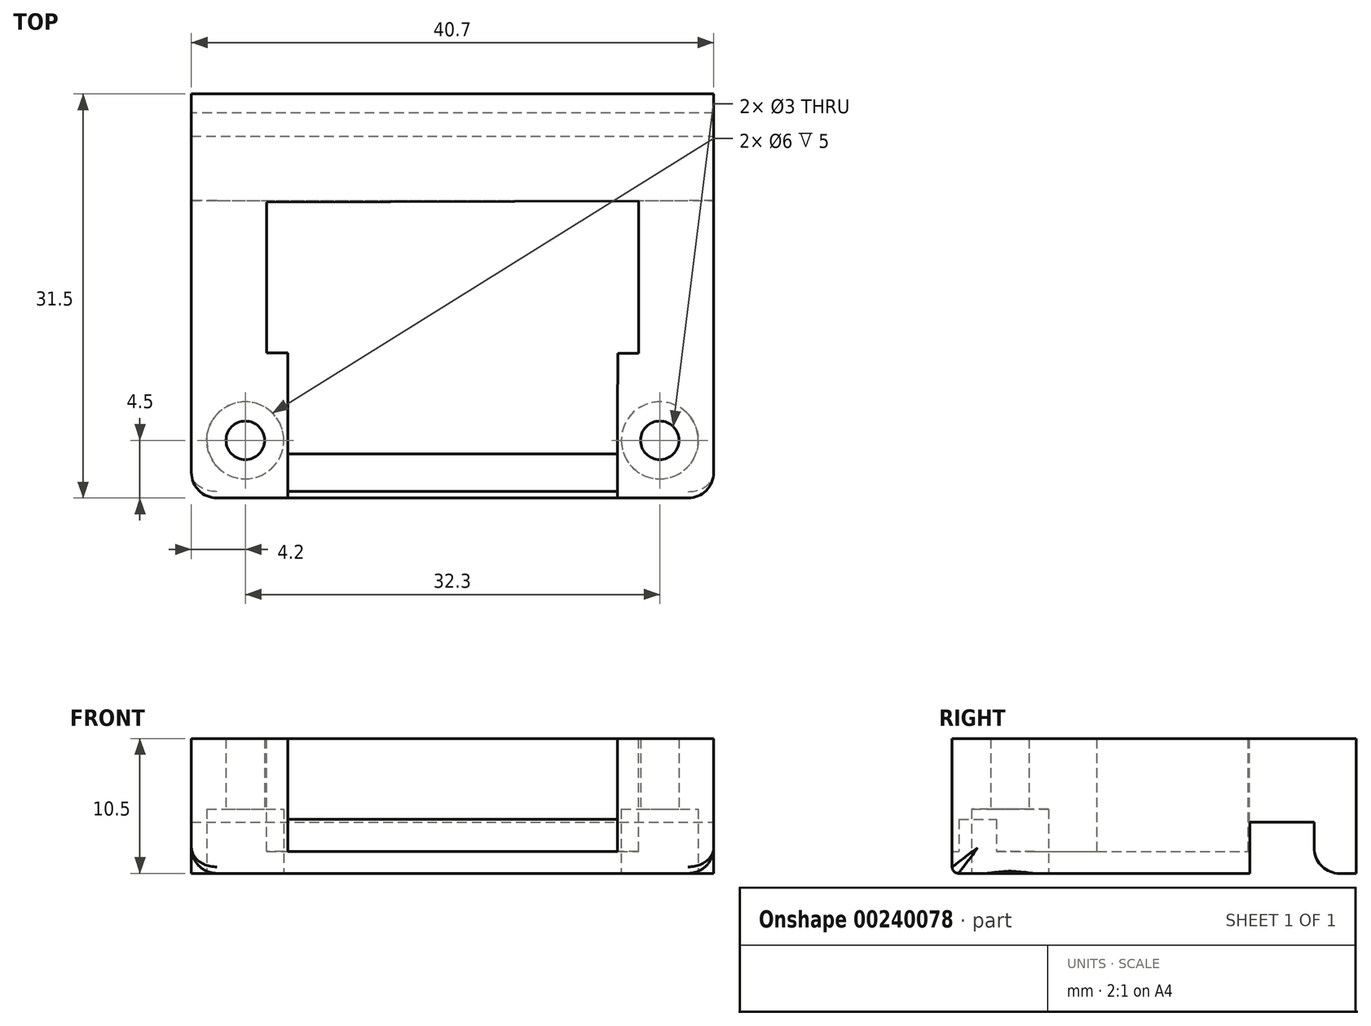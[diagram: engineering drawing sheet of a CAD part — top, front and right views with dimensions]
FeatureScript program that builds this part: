
annotation { "Feature Type Name" : "Feature", "Feature Type Description" : "" }
export const myFeature = defineFeature(function(context is Context, id is Id, definition is map)
    precondition{}
    {
        {
            var Q0;
            Q0=qCreatedBy(makeId("Top.planeOp"),FACE);
            var sketch = newSketch(context, id + "F0", { "sketchPlane" : qUnion([Q0])});
            skLineSegment(sketch, "E0.bottom", {"start": v(20.35, -15) * mm, "end": v(-20.35, -15) * mm});
            skLineSegment(sketch, "E0.top", {"start": v(20.35, 15) * mm, "end": v(-20.35, 15) * mm});
            skLineSegment(sketch, "E0.left", {"start": v(20.35, -15) * mm, "end": v(20.35, 15) * mm});
            skLineSegment(sketch, "E0.right", {"start": v(-20.35, -15) * mm, "end": v(-20.35, 15) * mm});
            skPoint(sketch, "E0.middle", {"position": v(0, 0) * mm});
            skPoint(sketch, "E1", {"position": v(16.15, -10.5) * mm});
            skPoint(sketch, "E2", {"position": v(-16.15, -10.5) * mm});
            skLineSegment(sketch, "E3", {"start": v(-20.35, 8.2) * mm, "end": v(20.35, 8.2) * mm});
            skLineSegment(sketch, "E4", {"start": v(-20.35, 13.2) * mm, "end": v(20.35, 13.2) * mm});
            skSolve(sketch);
        }
        {
            var Q0;
            Q0 = qSketchRegion(id + "F0", true);
            extrude(context, id + "F1", {"entities" : qUnion([Q0]), "depth" : 10.5 * mm});
        }
        {
            var Q0;
            Q0=sQuery(id+"F0.wireOp",VERTEX,"E2");
            var Q1;
            Q1=makeQuery(id+"F1.opExtrude","SWEPT_BODY",BODY,{"disambiguationData":[OSD([sQuery(id+"F0.wireOp",EDGE,"E0.bottom"),sQuery(id+"F0.wireOp",EDGE,"E0.top"),sQuery(id+"F0.wireOp",EDGE,"E0.left"),sQuery(id+"F0.wireOp",EDGE,"E0.right")])]});
            hole(context, id + "F2", {"style" : HoleStyle.C_BORE, "endStyle" : HoleEndStyle.THROUGH, "oppositeDirection" : true, "holeDiameter" : 3 * mm, "cBoreDiameter" : 6 * mm, "cBoreDepth" : 5 * mm, "locations" : qUnion([Q0]), "scope" : qUnion([Q1]), "isTappedThrough" : true});
        }
        {
            var Q0;
            Q0=sQuery(id+"F0.wireOp",VERTEX,"E1");
            var Q1;
            Q1=makeQuery(id+"F1.opExtrude","SWEPT_BODY",BODY,{"disambiguationData":[OSD([sQuery(id+"F0.wireOp",EDGE,"E0.bottom"),sQuery(id+"F0.wireOp",EDGE,"E0.top"),sQuery(id+"F0.wireOp",EDGE,"E0.left"),sQuery(id+"F0.wireOp",EDGE,"E0.right")])]});
            hole(context, id + "F3", {"style" : HoleStyle.C_BORE, "endStyle" : HoleEndStyle.THROUGH, "oppositeDirection" : true, "holeDiameter" : 3 * mm, "cBoreDiameter" : 6 * mm, "cBoreDepth" : 5 * mm, "locations" : qUnion([Q0]), "scope" : qUnion([Q1]), "isTappedThrough" : true});
        }
        {
            var Q0;
            {var subQ0=sQuery(id+"F0.wireOp",EDGE,"E3");Q0=makeQuery(id+"F0.imprint","IMPRINT",FACE,{"disambiguationData":[TD([[makeQuery(id+"F0.imprint","IMPRINT",EDGE,{"derivedFrom":subQ0}),1.0]])]});}
            extrude(context, id + "F4", {"entities" : qUnion([Q0]), "operationType" : NewBodyOperationType.REMOVE, "depth" : 4 * mm});
        }
        {
            var Q0;
            Q0=makeQuery(id+"F1.opExtrude","CAP_FACE",FACE,{"disambiguationData":[OSD([sQuery(id+"F0.wireOp",EDGE,"E0.bottom"),sQuery(id+"F0.wireOp",EDGE,"E0.top"),sQuery(id+"F0.wireOp",EDGE,"E0.left"),sQuery(id+"F0.wireOp",EDGE,"E0.right")])],"isStart":false});
            var sketch = newSketch(context, id + "F5", { "sketchPlane" : qUnion([Q0])});
            skLineSegment(sketch, "E5", {"start": v(-12.85, -8.67) * mm, "end": v(-12.85, -15) * mm});
            skLineSegment(sketch, "E6", {"start": v(12.85, -8.58) * mm, "end": v(12.85, -15) * mm});
            skLineSegment(sketch, "E7", {"start": v(-12.85, -8.67) * mm, "end": v(-20.35, -8.67) * mm});
            skLineSegment(sketch, "E8", {"start": v(12.85, -8.58) * mm, "end": v(20.35, -8.58) * mm});
            skLineSegment(sketch, "E9", {"start": v(14.5, 8.17) * mm, "end": v(-14.5, 8.08) * mm});
            skLineSegment(sketch, "E10", {"start": v(-12.85, -8.67) * mm, "end": v(-12.85, -3.7) * mm});
            skLineSegment(sketch, "E11", {"start": v(12.85, -8.58) * mm, "end": v(12.89, -3.7) * mm});
            skLineSegment(sketch, "E12", {"start": v(-14.5, -3.7) * mm, "end": v(-14.5, 8.08) * mm});
            skLineSegment(sketch, "E13", {"start": v(12.89, -3.7) * mm, "end": v(14.5, -3.72) * mm});
            skLineSegment(sketch, "E14", {"start": v(14.5, -3.72) * mm, "end": v(14.5, 8.17) * mm});
            skLineSegment(sketch, "E15", {"start": v(-14.5, -3.7) * mm, "end": v(-12.85, -3.7) * mm});
            skSolve(sketch);
        }
        {
            var Q0;
            {var subQ3=sQuery(id+"F5.wireOp",EDGE,"E5");Q0=makeQuery(id+"F5.imprint","IMPRINT",FACE,{"disambiguationData":[TD([[makeQuery(id+"F5.imprint","IMPRINT",EDGE,{"derivedFrom":subQ3}),1.0]])]});}
            extrude(context, id + "F6", {"entities" : qUnion([Q0]), "operationType" : NewBodyOperationType.REMOVE, "oppositeDirection" : true, "depth" : 8.8 * mm});
        }
        {
            var Q0;
            Q0=makeQuery(id+"F6.boolean.opBoolean","COPY",EDGE,{"derivedFrom":makeQuery(id+"F6.opExtrude","SWEPT_EDGE",EDGE,{"disambiguationData":[OSD([sQuery(id+"F0.wireOp",EDGE,"E0.bottom"),sQuery(id+"F5.wireOp",EDGE,"E5")])]})});
            var Q1;
            Q1=makeQuery(id+"F1.opExtrude","SWEPT_EDGE",EDGE,{"disambiguationData":[OSD([sQuery(id+"F0.wireOp",EDGE,"E0.bottom"),sQuery(id+"F0.wireOp",EDGE,"E0.right")])]});
            var Q2;
            Q2=makeQuery(id+"F1.opExtrude","SWEPT_EDGE",EDGE,{"disambiguationData":[OSD([sQuery(id+"F0.wireOp",EDGE,"E0.bottom"),sQuery(id+"F0.wireOp",EDGE,"E0.left")])]});
            var Q3;
            Q3=makeQuery(id+"F6.boolean.opBoolean","COPY",EDGE,{"derivedFrom":makeQuery(id+"F6.opExtrude","SWEPT_EDGE",EDGE,{"disambiguationData":[OSD([sQuery(id+"F0.wireOp",EDGE,"E0.bottom"),sQuery(id+"F5.wireOp",EDGE,"E6")])]})});
            var Q4;
            {var subQ0=sQuery(id+"F0.wireOp",EDGE,"E0.bottom");var subQ1=sQuery(id+"F0.wireOp",EDGE,"E0.right");Q4=makeQuery(id+"F4.boolean.opBoolean","SPLIT",EDGE,{"disambiguationData":[TD([makeQuery(id+"F1.opExtrude","SWEPT_FACE",FACE,{"disambiguationData":[OSD([subQ0])]})])],"derivedFrom":makeQuery(id+"F1.opExtrude","CAP_EDGE",EDGE,{"disambiguationData":[OSD([subQ1])],"isStart":true})});}
            var Q5;
            {var subQ0=sQuery(id+"F0.wireOp",EDGE,"E0.bottom");var subQ1=sQuery(id+"F0.wireOp",EDGE,"E0.left");Q5=makeQuery(id+"F4.boolean.opBoolean","SPLIT",EDGE,{"disambiguationData":[TD([makeQuery(id+"F1.opExtrude","SWEPT_FACE",FACE,{"disambiguationData":[OSD([subQ0])]})])],"derivedFrom":makeQuery(id+"F1.opExtrude","CAP_EDGE",EDGE,{"disambiguationData":[OSD([subQ1])],"isStart":true})});}
            var Q6;
            Q6=makeQuery(id+"F4.boolean.opBoolean","COPY",EDGE,{"derivedFrom":makeQuery(id+"F4.opExtrude","CAP_EDGE",EDGE,{"disambiguationData":[OSD([sQuery(id+"F0.wireOp",EDGE,"E4")])],"isStart":true})});
            var Q7;
            Q7=makeQuery(id+"F4.boolean.opBoolean","COPY",EDGE,{"derivedFrom":makeQuery(id+"F4.opExtrude","CAP_EDGE",EDGE,{"disambiguationData":[OSD([sQuery(id+"F0.wireOp",EDGE,"E3")])],"isStart":true})});
            var Q8;
            Q8=makeQuery(id+"F4.boolean.opBoolean","COPY",EDGE,{"derivedFrom":makeQuery(id+"F4.opExtrude","CAP_EDGE",EDGE,{"disambiguationData":[OSD([sQuery(id+"F0.wireOp",EDGE,"E0.left")])],"isStart":false})});
            var Q9;
            Q9=makeQuery(id+"F4.boolean.opBoolean","COPY",EDGE,{"derivedFrom":makeQuery(id+"F4.opExtrude","CAP_EDGE",EDGE,{"disambiguationData":[OSD([sQuery(id+"F0.wireOp",EDGE,"E0.right")])],"isStart":false})});
            fillet(context, id + "F7", {"entities" : qUnion([Q0, Q1, Q2, Q3, Q4, Q5, Q6, Q7, Q8, Q9]), "radius" : 2 * mm, "tangentPropagation" : true, "allowEdgeOverflow" : false});
        }
        {
            var Q0;
            Q0=makeQuery(id+"F1.opExtrude","CAP_EDGE",EDGE,{"disambiguationData":[OSD([sQuery(id+"F0.wireOp",EDGE,"E0.bottom")])],"isStart":true});
            var Q1;
            Q1=makeQuery(id+"F6.boolean.opBoolean","COPY",EDGE,{"derivedFrom":makeQuery(id+"F6.opExtrude","CAP_EDGE",EDGE,{"disambiguationData":[OSD([sQuery(id+"F0.wireOp",EDGE,"E0.bottom")])],"isStart":false})});
            fillet(context, id + "F8", {"entities" : qUnion([Q0, Q1]), "radius" : .5 * mm, "tangentPropagation" : true, "allowEdgeOverflow" : false});
        }
        {
            var Q0;
            Q0=makeQuery(id+"F6.boolean.opBoolean","COPY",FACE,{"derivedFrom":makeQuery(id+"F6.opExtrude","CAP_FACE",FACE,{"disambiguationData":[OSD([sQuery(id+"F0.wireOp",EDGE,"E0.bottom"),sQuery(id+"F5.wireOp",EDGE,"E5"),sQuery(id+"F5.wireOp",EDGE,"E6"),sQuery(id+"F5.wireOp",EDGE,"E10"),sQuery(id+"F5.wireOp",EDGE,"E11"),sQuery(id+"F5.wireOp",EDGE,"E12"),sQuery(id+"F5.wireOp",EDGE,"E13"),sQuery(id+"F5.wireOp",EDGE,"E14"),sQuery(id+"F5.wireOp",EDGE,"E9"),sQuery(id+"F5.wireOp",EDGE,"E15")])],"isStart":false})});
            var sketch = newSketch(context, id + "F9", { "sketchPlane" : qUnion([Q0])});
            skLineSegment(sketch, "E16.bottom", {"start": v(-13.59, -11.54) * mm, "end": v(14.21, -11.54) * mm});
            skLineSegment(sketch, "E16.top", {"start": v(-13.59, -14.47) * mm, "end": v(14.21, -14.47) * mm});
            skLineSegment(sketch, "E16.left", {"start": v(-13.59, -11.54) * mm, "end": v(-13.59, -14.47) * mm});
            skLineSegment(sketch, "E16.right", {"start": v(14.21, -11.54) * mm, "end": v(14.21, -14.47) * mm});
            skSolve(sketch);
        }
        {
            var Q0;
            {var subQ1=sQuery(id+"F5.wireOp",EDGE,"E6");var subQ6=makeQuery(id+"F6.boolean.opBoolean","COPY",EDGE,{"derivedFrom":makeQuery(id+"F6.opExtrude","CAP_EDGE",EDGE,{"disambiguationData":[OSD([subQ1])],"isStart":false})});var subQ8=sQuery(id+"F9.wireOp",EDGE,"E16.bottom");var subQ9=makeQuery(id+"F9.imprint","INTERSECT",VERTEX,{"derivedFrom":[subQ6,subQ8]});Q0=makeQuery(id+"F9.imprint","IMPRINT",FACE,{"disambiguationData":[TD([[makeQuery(id+"F9.imprint","IMPRINT",EDGE,{"disambiguationData":[TD([[subQ9,1.0]])],"derivedFrom":subQ8}),-1.0]])]});}
            extrude(context, id + "F10", {"entities" : qUnion([Q0]), "operationType" : NewBodyOperationType.ADD, "depth" : 2.5 * mm});
        }
        {
            var Q0;
            Q0=makeQuery(id+"F1.opExtrude","SWEPT_FACE",FACE,{"disambiguationData":[OSD([sQuery(id+"F0.wireOp",EDGE,"E0.top")])]});
            extrude(context, id + "F11", {"entities" : qUnion([Q0]), "operationType" : NewBodyOperationType.ADD, "depth" : 1.5 * mm});
        }
    });
